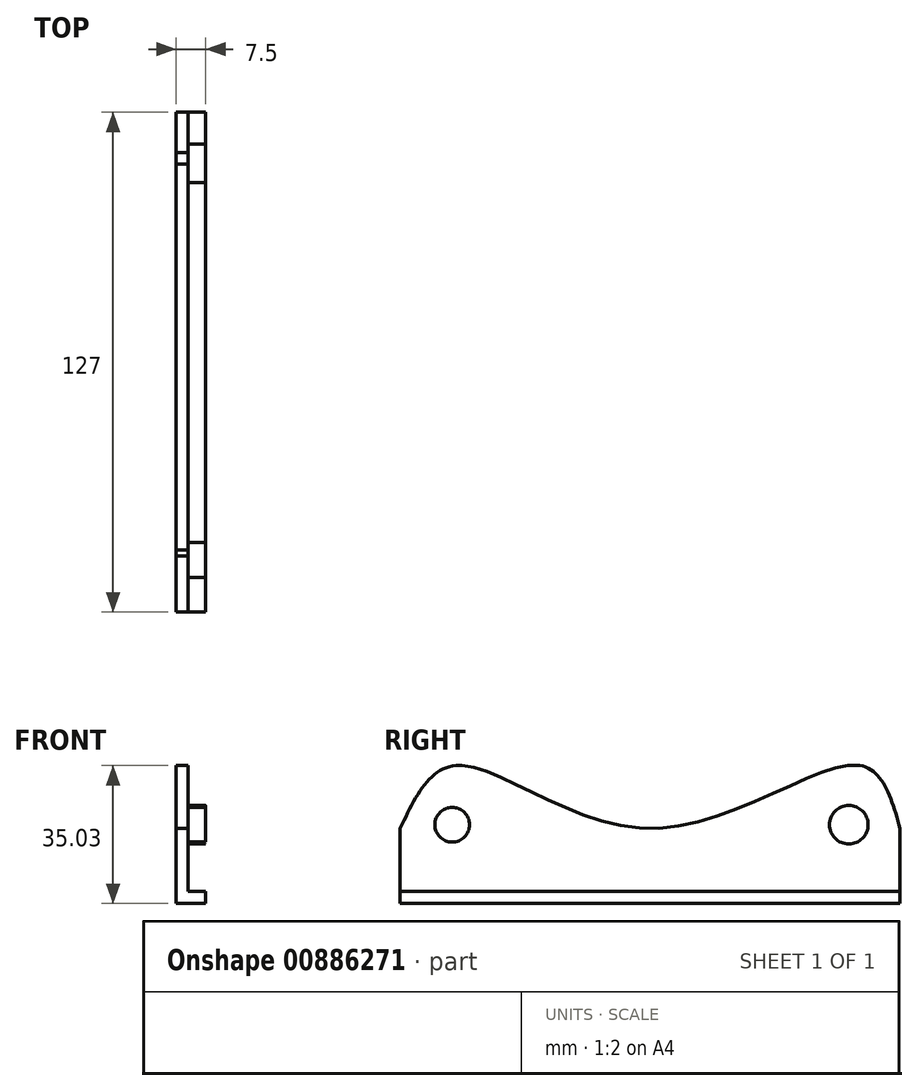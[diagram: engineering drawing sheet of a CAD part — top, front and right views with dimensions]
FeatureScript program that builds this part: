
annotation { "Feature Type Name" : "Feature", "Feature Type Description" : "" }
export const myFeature = defineFeature(function(context is Context, id is Id, definition is map)
    precondition{}
    {
        {
            var Q0;
            Q0=qCreatedBy(makeId("Front.planeOp"),FACE);
            var sketch = newSketch(context, id + "F0", { "sketchPlane" : qUnion([Q0])});
            skLineSegment(sketch, "E0", {"start": v(0, 0) * mm, "end": v(0, 35.03) * mm});
            skLineSegment(sketch, "E1", {"start": v(0, 35.03) * mm, "end": v(2.99, 35.03) * mm});
            skLineSegment(sketch, "E2", {"start": v(2.99, 35.03) * mm, "end": v(2.99, 3) * mm});
            skLineSegment(sketch, "E3", {"start": v(2.99, 3) * mm, "end": v(7.5, 3) * mm});
            skLineSegment(sketch, "E4", {"start": v(7.5, 3) * mm, "end": v(7.5, 0) * mm});
            skLineSegment(sketch, "E5", {"start": v(7.5, 0) * mm, "end": v(0, 0) * mm});
            skSolve(sketch);
        }
        {
            var Q0;
            Q0=makeQuery(id+"F0.imprint","IMPRINT",FACE,{"disambiguationData":[TD([[makeQuery(id+"F0.imprint","IMPRINT",EDGE,{"derivedFrom":sQuery(id+"F0.wireOp",EDGE,"E0")}),-1.0]])]});
            extrude(context, id + "F1", {"entities" : qUnion([Q0]), "depth" : 127 * mm, "offsetDistance" : 25 * mm});
        }
        {
            var Q0;
            Q0=makeQuery(id+"F1.opExtrude","SWEPT_FACE",FACE,{"disambiguationData":[OSD([sQuery(id+"F0.wireOp",EDGE,"E2")])]});
            var sketch = newSketch(context, id + "F2", { "sketchPlane" : qUnion([Q0])});
            skCircle(sketch, "E6", {"center": v(-113.77, 20) * mm, "radius": 4.41 * mm});
            skCircle(sketch, "E7", {"center": v(-13, 20) * mm, "radius": 4.9 * mm});
            skSolve(sketch);
        }
        {
            var Q0;
            Q0=makeQuery(id+"F2.imprint","IMPRINT",FACE,{"disambiguationData":[TD([[makeQuery(id+"F2.imprint","IMPRINT",EDGE,{"derivedFrom":sQuery(id+"F2.wireOp",EDGE,"E6")}),1.0]])]});
            var Q1;
            Q1=makeQuery(id+"F2.imprint","IMPRINT",FACE,{"disambiguationData":[TD([[makeQuery(id+"F2.imprint","IMPRINT",EDGE,{"derivedFrom":sQuery(id+"F2.wireOp",EDGE,"E7")}),1.0]])]});
            extrude(context, id + "F3", {"entities" : qUnion([Q0, Q1]), "operationType" : NewBodyOperationType.ADD, "depth" : 4.5 * mm, "offsetDistance" : 25 * mm});
        }
        {
            var Q0;
            Q0=makeQuery(id+"F1.opExtrude","SWEPT_FACE",FACE,{"disambiguationData":[OSD([sQuery(id+"F0.wireOp",EDGE,"E2")])]});
            var sketch = newSketch(context, id + "F4", { "sketchPlane" : qUnion([Q0])});
            skPoint(sketch, "E8.2.internal.snap0", {"position": v(-63.5, 3) * mm});
            skPoint(sketch, "E8.2.internal.snap1", {"position": v(-127, 19.01) * mm});
            skFitSpline(sketch, "E8", {"points": [v(-127, 19.01) * mm, v(-112.81, 35.03) * mm, v(-63.5, 19.01) * mm, v(-10.25, 35.03) * mm, v(0, 19.01) * mm], "startDerivative": vector(55.9, 118.84) * mm, "endDerivative": vector(33.8, -122.67) * mm});
            skLineSegment(sketch, "E9", {"start": v(-127, 19.01) * mm, "end": v(-127, 35.03) * mm});
            skLineSegment(sketch, "E10", {"start": v(-127, 35.03) * mm, "end": v(0, 35.03) * mm});
            skLineSegment(sketch, "E11", {"start": v(0, 35.03) * mm, "end": v(0, 19.01) * mm});
            skSolve(sketch);
        }
        {
            var Q0;
            {var subQ0=sQuery(id+"F4.wireOp",EDGE,"E10");var subQ1=sQuery(id+"F4.wireOp",EDGE,"E8");var subQ2=makeQuery(id+"F4.imprint","INTERSECT",VERTEX,{"disambiguationData":[OD(1.0)],"derivedFrom":[subQ1,subQ0]});Q0=makeQuery(id+"F4.imprint","IMPRINT",FACE,{"disambiguationData":[TD([[makeQuery(id+"F4.imprint","IMPRINT",EDGE,{"disambiguationData":[TD([[subQ2,-1.0]])],"derivedFrom":subQ1}),1.0]])]});}
            var Q1;
            {var subQ0=sQuery(id+"F4.wireOp",EDGE,"E9");Q1=makeQuery(id+"F4.imprint","IMPRINT",FACE,{"disambiguationData":[TD([[makeQuery(id+"F4.imprint","IMPRINT",EDGE,{"derivedFrom":subQ0}),1.0]])]});}
            var Q2;
            {var subQ0=sQuery(id+"F4.wireOp",EDGE,"E11");Q2=makeQuery(id+"F4.imprint","IMPRINT",FACE,{"disambiguationData":[TD([[makeQuery(id+"F4.imprint","IMPRINT",EDGE,{"derivedFrom":subQ0}),-1.0]])]});}
            extrude(context, id + "F5", {"entities" : qUnion([Q0, Q1, Q2]), "operationType" : NewBodyOperationType.REMOVE, "oppositeDirection" : true, "depth" : 25 * mm, "offsetDistance" : 25 * mm});
        }
    });
